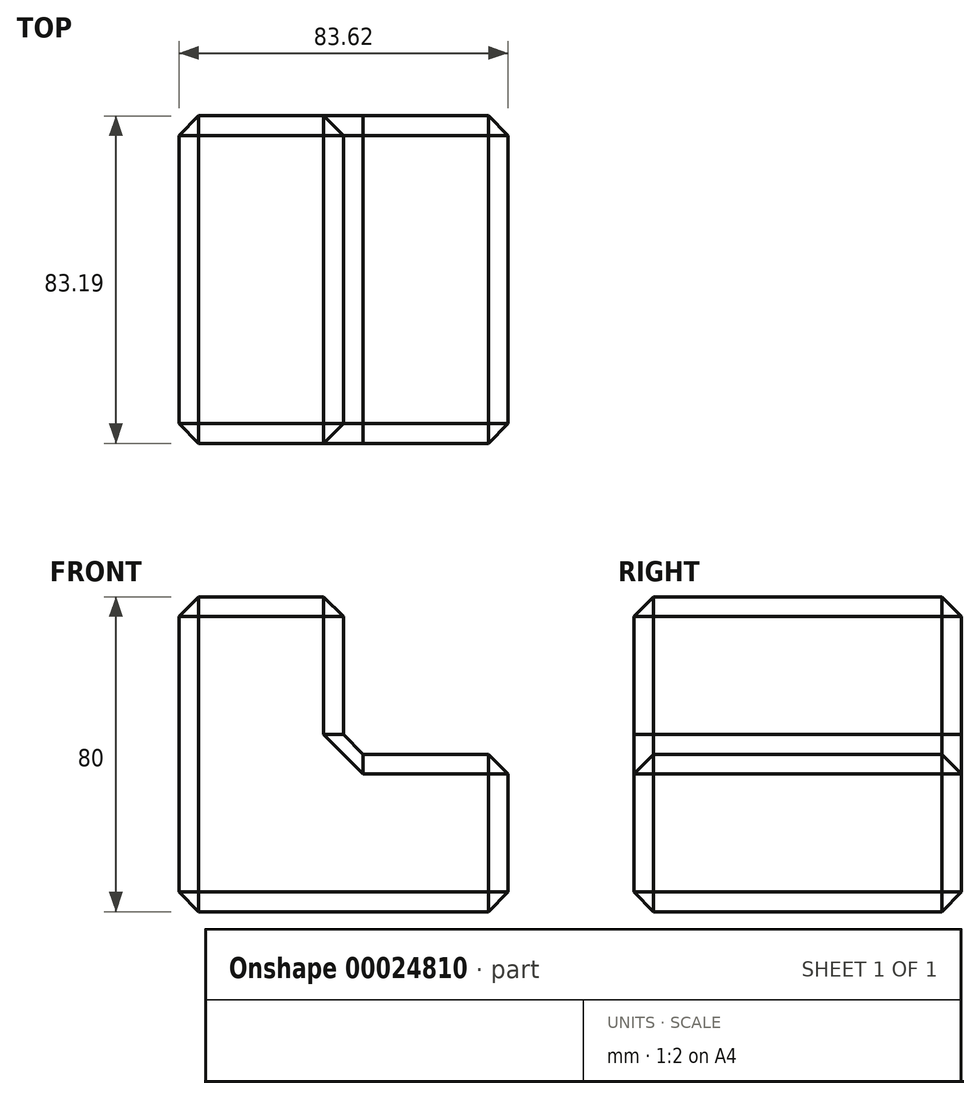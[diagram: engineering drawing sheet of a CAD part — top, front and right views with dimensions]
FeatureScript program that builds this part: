
annotation { "Feature Type Name" : "Feature", "Feature Type Description" : "" }
export const myFeature = defineFeature(function(context is Context, id is Id, definition is map)
    precondition{}
    {
        {
            var Q0;
            Q0=qCreatedBy(makeId("Top.planeOp"),FACE);
            var sketch = newSketch(context, id + "F0", { "sketchPlane" : qUnion([Q0])});
            skLineSegment(sketch, "E0.bottom", {"start": v(-59.13, -45.93) * mm, "end": v(24.5, -45.93) * mm});
            skLineSegment(sketch, "E0.top", {"start": v(-59.13, 37.26) * mm, "end": v(24.5, 37.26) * mm});
            skLineSegment(sketch, "E0.left", {"start": v(-59.13, -45.93) * mm, "end": v(-59.13, 37.26) * mm});
            skLineSegment(sketch, "E0.right", {"start": v(24.5, -45.93) * mm, "end": v(24.5, 37.26) * mm});
            skSolve(sketch);
        }
        {
            var Q0;
            Q0=makeQuery(id+"F0.imprint","IMPRINT",FACE,{"disambiguationData":[TD([[makeQuery(id+"F0.imprint","IMPRINT",EDGE,{"derivedFrom":sQuery(id+"F0.wireOp",EDGE,"E0.bottom")}),1.0]])]});
            extrude(context, id + "F1", {"entities" : qUnion([Q0]), "depth" : 40 * mm});
        }
        {
            var Q0;
            Q0=makeQuery(id+"F1.opExtrude","CAP_FACE",FACE,{"disambiguationData":[OSD([sQuery(id+"F0.wireOp",EDGE,"E0.bottom"),sQuery(id+"F0.wireOp",EDGE,"E0.top"),sQuery(id+"F0.wireOp",EDGE,"E0.left"),sQuery(id+"F0.wireOp",EDGE,"E0.right")])],"isStart":false});
            var sketch = newSketch(context, id + "F2", { "sketchPlane" : qUnion([Q0])});
            skLineSegment(sketch, "E1", {"start": v(-17.32, 37.26) * mm, "end": v(-17.32, -45.93) * mm});
            skSolve(sketch);
        }
        {
            var Q0;
            {var subQ1=sQuery(id+"F2.wireOp",EDGE,"E1");Q0=makeQuery(id+"F2.imprint","IMPRINT",FACE,{"disambiguationData":[TD([[makeQuery(id+"F2.imprint","IMPRINT",EDGE,{"derivedFrom":subQ1}),-1.0]])]});}
            extrude(context, id + "F3", {"entities" : qUnion([Q0]), "operationType" : NewBodyOperationType.ADD, "depth" : 40 * mm});
        }
        {
            var Q0;
            Q0=makeQuery(id+"F3.opExtrude","CAP_FACE",FACE,{"disambiguationData":[OSD([sQuery(id+"F0.wireOp",EDGE,"E0.bottom"),sQuery(id+"F0.wireOp",EDGE,"E0.top"),sQuery(id+"F0.wireOp",EDGE,"E0.left"),sQuery(id+"F2.wireOp",EDGE,"E1")])],"isStart":false});
            var Q1;
            {var subQ0=sQuery(id+"F0.wireOp",EDGE,"E0.bottom");Q1=makeQuery(id+"F3.boolean.opBoolean","MERGE",FACE,{"derivedFrom":[makeQuery(id+"F1.opExtrude","SWEPT_FACE",FACE,{"disambiguationData":[OSD([subQ0])]}),makeQuery(id+"F3.opExtrude","SWEPT_FACE",FACE,{"disambiguationData":[OSD([subQ0])]})]});}
            var Q2;
            Q2=makeQuery(id+"F3.opExtrude","SWEPT_FACE",FACE,{"disambiguationData":[OSD([sQuery(id+"F2.wireOp",EDGE,"E1")])]});
            var Q3;
            Q3=makeQuery(id+"F1.opExtrude","CAP_FACE",FACE,{"disambiguationData":[OSD([sQuery(id+"F0.wireOp",EDGE,"E0.bottom"),sQuery(id+"F0.wireOp",EDGE,"E0.top"),sQuery(id+"F0.wireOp",EDGE,"E0.left"),sQuery(id+"F0.wireOp",EDGE,"E0.right")])],"isStart":false});
            var Q4;
            Q4=makeQuery(id+"F1.opExtrude","SWEPT_FACE",FACE,{"disambiguationData":[OSD([sQuery(id+"F0.wireOp",EDGE,"E0.right")])]});
            var Q5;
            {var subQ0=sQuery(id+"F0.wireOp",EDGE,"E0.top");Q5=makeQuery(id+"F3.boolean.opBoolean","MERGE",FACE,{"derivedFrom":[makeQuery(id+"F1.opExtrude","SWEPT_FACE",FACE,{"disambiguationData":[OSD([subQ0])]}),makeQuery(id+"F3.opExtrude","SWEPT_FACE",FACE,{"disambiguationData":[OSD([subQ0])]})]});}
            var Q6;
            {var subQ0=sQuery(id+"F0.wireOp",EDGE,"E0.left");Q6=makeQuery(id+"F3.boolean.opBoolean","MERGE",FACE,{"derivedFrom":[makeQuery(id+"F1.opExtrude","SWEPT_FACE",FACE,{"disambiguationData":[OSD([subQ0])]}),makeQuery(id+"F3.opExtrude","SWEPT_FACE",FACE,{"disambiguationData":[OSD([subQ0])]})]});}
            var Q7;
            Q7=makeQuery(id+"F1.opExtrude","CAP_FACE",FACE,{"disambiguationData":[OSD([sQuery(id+"F0.wireOp",EDGE,"E0.bottom"),sQuery(id+"F0.wireOp",EDGE,"E0.top"),sQuery(id+"F0.wireOp",EDGE,"E0.left"),sQuery(id+"F0.wireOp",EDGE,"E0.right")])],"isStart":true});
            chamfer(context, id + "F4", {"entities" : qUnion([Q0, Q1, Q2, Q3, Q4, Q5, Q6, Q7]), "width" : 5 * mm, "tangentPropagation" : true});
        }
    });
